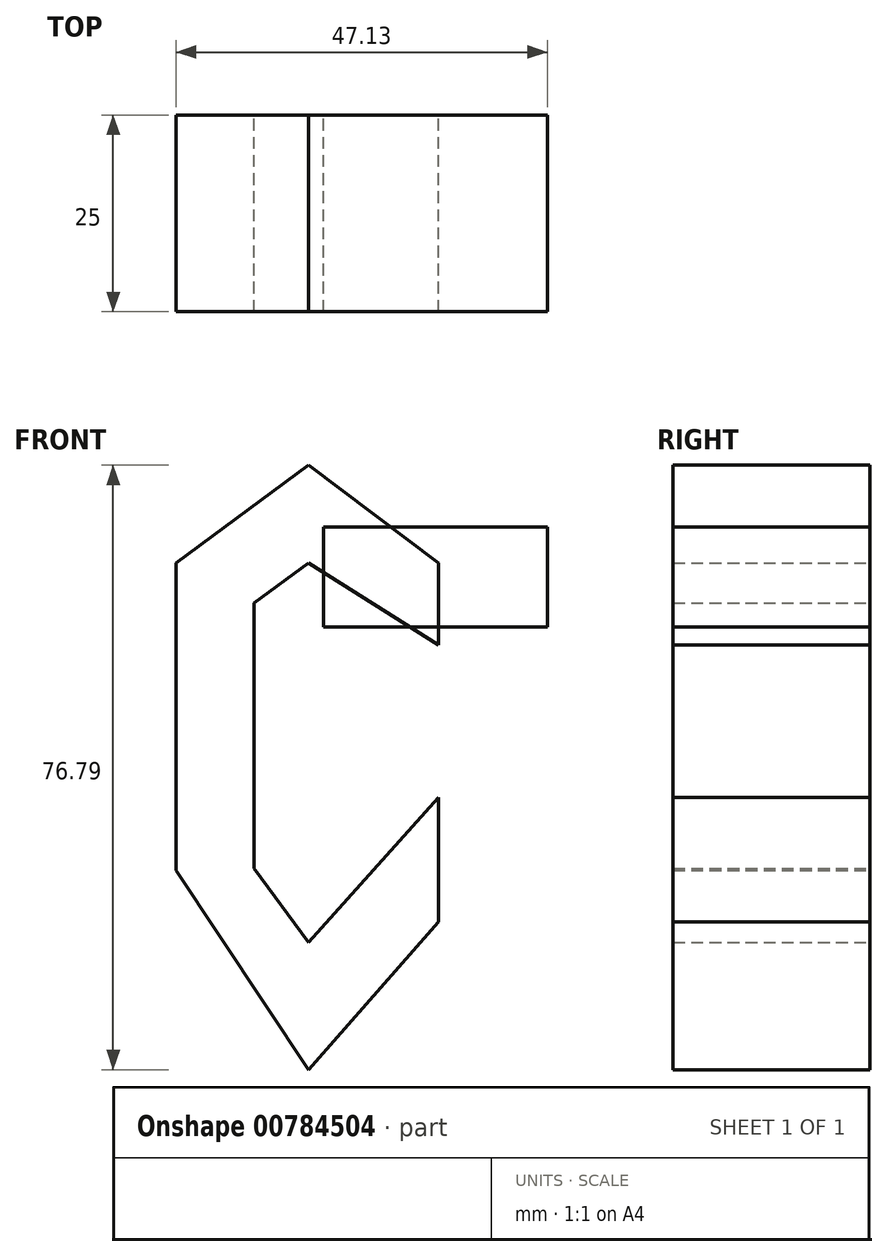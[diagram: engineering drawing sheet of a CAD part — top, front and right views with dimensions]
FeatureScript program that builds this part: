
annotation { "Feature Type Name" : "Feature", "Feature Type Description" : "" }
export const myFeature = defineFeature(function(context is Context, id is Id, definition is map)
    precondition{}
    {
        {
            var Q0;
            Q0=qCreatedBy(makeId("Front.planeOp"),FACE);
            var sketch = newSketch(context, id + "F0", { "sketchPlane" : qUnion([Q0])});
            skLineSegment(sketch, "E0", {"start": v(-9.92, 0) * mm, "end": v(-9.92, 23.56) * mm});
            skLineSegment(sketch, "E1", {"start": v(-9.92, 23.56) * mm, "end": v(6.9, 35.96) * mm});
            skLineSegment(sketch, "E2", {"start": v(6.9, 35.96) * mm, "end": v(23.38, 23.56) * mm});
            skLineSegment(sketch, "E3", {"start": v(23.38, 23.56) * mm, "end": v(23.38, 13.1) * mm});
            skLineSegment(sketch, "E4", {"start": v(23.38, 13.1) * mm, "end": v(6.9, 23.56) * mm});
            skLineSegment(sketch, "E5", {"start": v(6.9, 23.56) * mm, "end": v(0, 18.47) * mm});
            skLineSegment(sketch, "E6", {"start": v(0, 18.47) * mm, "end": v(0, -15.28) * mm});
            skLineSegment(sketch, "E7", {"start": v(0, -15.28) * mm, "end": v(6.9, -24.65) * mm});
            skLineSegment(sketch, "E8", {"start": v(6.9, -24.65) * mm, "end": v(23.38, -6.26) * mm});
            skLineSegment(sketch, "E9", {"start": v(23.38, -6.26) * mm, "end": v(23.38, -22.04) * mm});
            skLineSegment(sketch, "E10", {"start": v(23.38, -22.04) * mm, "end": v(6.9, -40.83) * mm});
            skLineSegment(sketch, "E11", {"start": v(6.9, -40.83) * mm, "end": v(-9.92, -15.53) * mm});
            skLineSegment(sketch, "E12", {"start": v(-9.92, -15.53) * mm, "end": v(-9.92, 0) * mm});
            skLineSegment(sketch, "E13.bottom", {"start": v(37.3, 28.12) * mm, "end": v(65.71, 28.12) * mm});
            skLineSegment(sketch, "E13.top", {"start": v(37.3, 15.4) * mm, "end": v(65.71, 15.4) * mm});
            skLineSegment(sketch, "E13.left", {"start": v(37.3, 28.12) * mm, "end": v(37.3, 15.4) * mm});
            skLineSegment(sketch, "E13.right", {"start": v(65.71, 28.12) * mm, "end": v(65.71, 15.4) * mm});
            skSolve(sketch);
        }
        {
            var Q0;
            Q0=makeQuery(id+"F0.imprint","IMPRINT",FACE,{"disambiguationData":[TD([[makeQuery(id+"F0.imprint","IMPRINT",EDGE,{"derivedFrom":sQuery(id+"F0.wireOp",EDGE,"E0")}),-1.0]])]});
            extrude(context, id + "F1", {"entities" : qUnion([Q0]), "depth" : 5.3 * mm, "offsetDistance" : 25 * mm});
        }
        {
            var Q0;
            Q0=makeQuery(id+"F1.opExtrude","CAP_EDGE",EDGE,{"disambiguationData":[OSD([sQuery(id+"F0.wireOp",EDGE,"E0"),sQuery(id+"F0.wireOp",EDGE,"E12")])],"isStart":false});
            var Q1;
            Q1=makeQuery(id+"F1.opExtrude","CAP_EDGE",EDGE,{"disambiguationData":[OSD([sQuery(id+"F0.wireOp",EDGE,"E11")])],"isStart":false});
            var Q2;
            Q2=makeQuery(id+"F1.opExtrude","CAP_EDGE",EDGE,{"disambiguationData":[OSD([sQuery(id+"F0.wireOp",EDGE,"E10")])],"isStart":false});
            var Q3;
            Q3=makeQuery(id+"F1.opExtrude","CAP_EDGE",EDGE,{"disambiguationData":[OSD([sQuery(id+"F0.wireOp",EDGE,"E9")])],"isStart":false});
            var Q4;
            Q4=makeQuery(id+"F1.opExtrude","CAP_EDGE",EDGE,{"disambiguationData":[OSD([sQuery(id+"F0.wireOp",EDGE,"E8")])],"isStart":false});
            var Q5;
            Q5=makeQuery(id+"F1.opExtrude","CAP_EDGE",EDGE,{"disambiguationData":[OSD([sQuery(id+"F0.wireOp",EDGE,"E7")])],"isStart":false});
            var Q6;
            Q6=makeQuery(id+"F1.opExtrude","CAP_EDGE",EDGE,{"disambiguationData":[OSD([sQuery(id+"F0.wireOp",EDGE,"E6")])],"isStart":false});
            var Q7;
            Q7=makeQuery(id+"F1.opExtrude","CAP_EDGE",EDGE,{"disambiguationData":[OSD([sQuery(id+"F0.wireOp",EDGE,"E5")])],"isStart":false});
            var Q8;
            Q8=makeQuery(id+"F1.opExtrude","CAP_EDGE",EDGE,{"disambiguationData":[OSD([sQuery(id+"F0.wireOp",EDGE,"E4")])],"isStart":false});
            var Q9;
            Q9=makeQuery(id+"F1.opExtrude","CAP_EDGE",EDGE,{"disambiguationData":[OSD([sQuery(id+"F0.wireOp",EDGE,"E3")])],"isStart":false});
            var Q10;
            Q10=makeQuery(id+"F1.opExtrude","CAP_EDGE",EDGE,{"disambiguationData":[OSD([sQuery(id+"F0.wireOp",EDGE,"E2")])],"isStart":false});
            var Q11;
            Q11=makeQuery(id+"F1.opExtrude","CAP_EDGE",EDGE,{"disambiguationData":[OSD([sQuery(id+"F0.wireOp",EDGE,"E1")])],"isStart":false});
            chamfer(context, id + "F2", {"entities" : qUnion([Q0, Q1, Q2, Q3, Q4, Q5, Q6, Q7, Q8, Q9, Q10, Q11]), "width" : 2 * mm, "tangentPropagation" : true});
        }
        {
            var Q0;
            Q0 = qSketchRegion(id + "F0", true);
            extrude(context, id + "F3", {"entities" : qUnion([Q0]), "operationType" : NewBodyOperationType.ADD, "depth" : 25 * mm, "offsetDistance" : 25 * mm});
        }
        {
            var Q0;
            Q0=makeQuery(id+"F3.opExtrude","SWEPT_BODY",BODY,{"disambiguationData":[OSD([sQuery(id+"F0.wireOp",EDGE,"E13.bottom"),sQuery(id+"F0.wireOp",EDGE,"E13.top"),sQuery(id+"F0.wireOp",EDGE,"E13.left"),sQuery(id+"F0.wireOp",EDGE,"E13.right")])]});
            transform(context, id + "F4", {"entities" : qUnion([Q0]), "transformType" : TransformType.TRANSLATION_3D, "dx" : -28.5 * mm, "dy" : 0 * mm, "dz" : 0 * mm, "makeCopy" : false});
        }
    });
